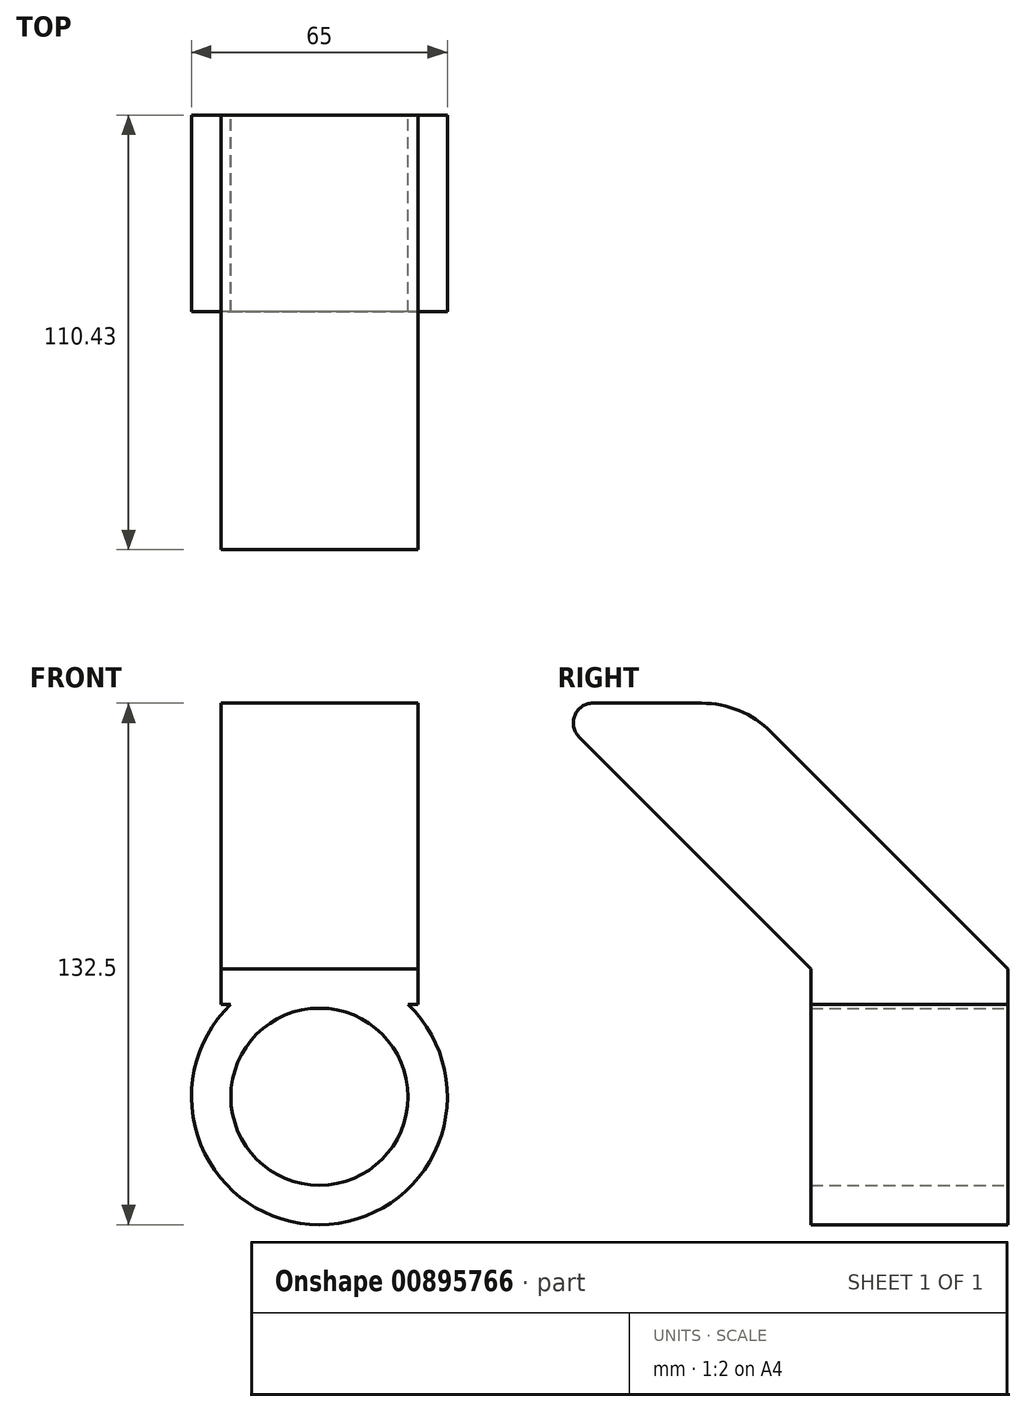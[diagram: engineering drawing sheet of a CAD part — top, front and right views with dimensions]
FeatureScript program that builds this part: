
annotation { "Feature Type Name" : "Feature", "Feature Type Description" : "" }
export const myFeature = defineFeature(function(context is Context, id is Id, definition is map)
    precondition{}
    {
        {
            var Q0;
            Q0=qCreatedBy(makeId("Front.planeOp"),FACE);
            var sketch = newSketch(context, id + "F0", { "sketchPlane" : qUnion([Q0])});
            skCircle(sketch, "E0", {"center": v(0, 0) * mm, "radius": 32.5 * mm});
            skCircle(sketch, "E1", {"center": v(0, 0) * mm, "radius": 22.5 * mm});
            skSolve(sketch);
        }
        {
            var Q0;
            Q0 = qSketchRegion(id + "F0", true);
            extrude(context, id + "F1", {"entities" : qUnion([Q0]), "depth" : 50 * mm, "offsetDistance" : 25 * mm});
        }
        {
            var Q0;
            Q0=qCreatedBy(makeId("Right.planeOp"),FACE);
            var sketch = newSketch(context, id + "F2", { "sketchPlane" : qUnion([Q0])});
            skLineSegment(sketch, "E2", {"start": v(0, 32.5) * mm, "end": v(-60.18, 92.68) * mm});
            skLineSegment(sketch, "E3", {"start": v(-77.86, 100) * mm, "end": v(-105.43, 100) * mm});
            skLineSegment(sketch, "E4", {"start": v(-108.96, 91.46) * mm, "end": v(-50, 32.5) * mm});
            skPoint(sketch, "E5.visualSharp", {"position": v(-67.5, 100) * mm});
            skArc(sketch, "E5.filletArc", {"start": v(-60.18, 92.68) * mm, "mid": v(-68.29, 98.1) * mm, "end": v(-77.86, 100) * mm});
            skPoint(sketch, "E6.visualSharp", {"position": v(-117.5, 100) * mm});
            skArc(sketch, "E6.filletArc", {"start": v(-105.43, 100) * mm, "mid": v(-110.05, 96.91) * mm, "end": v(-108.96, 91.46) * mm});
            skLineSegment(sketch, "E7", {"start": v(0, 32.5) * mm, "end": v(-50, 32.5) * mm});
            skSolve(sketch);
        }
        {
            var Q0;
            Q0 = qSketchRegion(id + "F2", true);
            extrude(context, id + "F3", {"entities" : qUnion([Q0]), "operationType" : NewBodyOperationType.ADD, "depth" : 25 * mm, "offsetDistance" : 25 * mm, "hasSecondDirection" : true, "secondDirectionOppositeDirection" : true, "secondDirectionDepth" : 25 * mm});
        }
        {
            var Q0;
            Q0=makeQuery(id+"F3.opExtrude","SWEPT_FACE",FACE,{"disambiguationData":[OSD([sQuery(id+"F2.wireOp",EDGE,"E7")])]});
            extrude(context, id + "F4", {"entities" : qUnion([Q0]), "operationType" : NewBodyOperationType.ADD, "depth" : 9.1 * mm, "offsetDistance" : 25 * mm});
        }
    });
